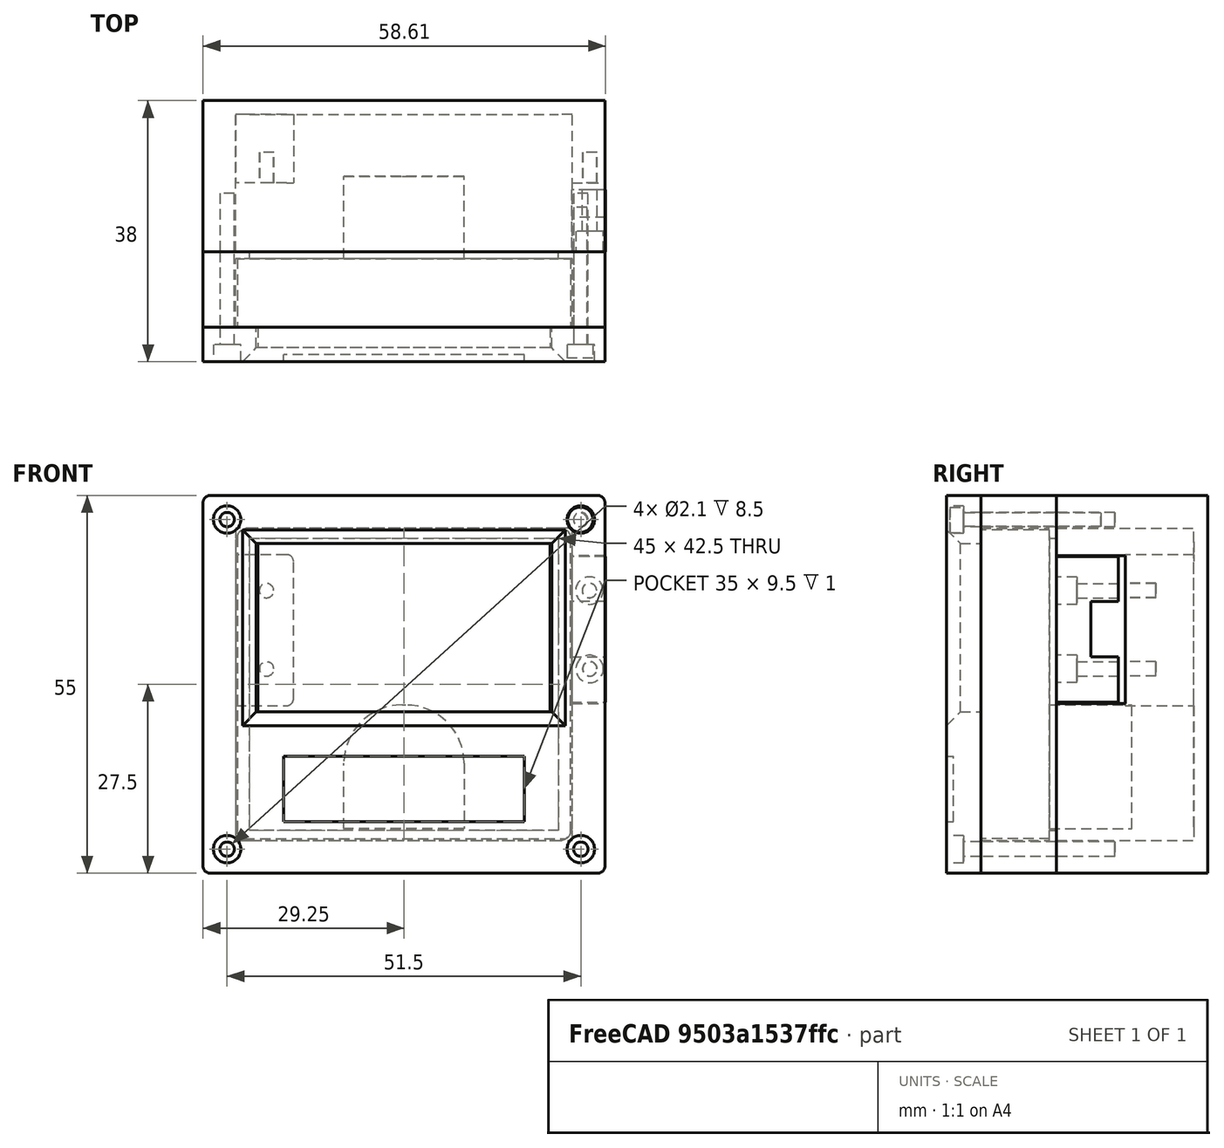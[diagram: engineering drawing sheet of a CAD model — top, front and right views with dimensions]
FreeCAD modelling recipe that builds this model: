
FCSTD DOCUMENT  (FreeCAD 0.21R33668 +26 (Git))
Label: nuvu-enclosure
License: All rights reserved
LicenseURL: http://en.wikipedia.org/wiki/All_rights_reserved
objects: Sketcher::SketchObject×24, PartDesign::Pocket×14, PartDesign::Pad×10, PartDesign::Fillet×8, PartDesign::Body×6, Mesh::Feature×2, PartDesign::Chamfer×1
note: 96 computed .brp shape members not serialized (recipe doc carries the construction recipe); baked Part::Feature solids carry a one-line shape summary decoded from their .brp

FEATURE [Sketcher::SketchObject] Sketch002
  FullyConstrained = true
  MapMode = 5
  Placement = pos=(0,0,0) rot=(1,0,0;1.5708rad)
  Support = -> [XZ_Plane]
  sketch-geometry (5):
    g0: LineSegment StartX=-24.25 StartY=22.5 StartZ=0 EndX=-24.25 EndY=-22.5 EndZ=0
    g1: LineSegment StartX=-24.25 StartY=-22.5 StartZ=0 EndX=24.25 EndY=-22.5 EndZ=0
    g2: LineSegment StartX=24.25 StartY=-22.5 StartZ=0 EndX=24.25 EndY=22.5 EndZ=0
    g3: LineSegment StartX=24.25 StartY=22.5 StartZ=0 EndX=-24.25 EndY=22.5 EndZ=0
    g4: GeomPoint X=0 Y=0 Z=0
  constraints (12):
    c: Coincident(g0,g1)
    c: Coincident(g1,g2)
    c: Coincident(g2,g3)
    c: Coincident(g3,g0)
    c: Horizontal(g1)
    c: Horizontal(g3)
    c: Vertical(g0)
    c: Vertical(g2)
    c: Symmetric(g1,g0,g4)
    c: Coincident(g4,g-1)
    c: DistanceY(g0,g0) = 45
    c: DistanceX(g3,g3) = 48.5
FEATURE [PartDesign::Pad] Pad
  Direction = (0,-1,-2e-16)
  Length = 10
  Length2 = 10
  Placement = pos=(0,0,0) rot=(1,0,0;1.5708rad)
  Profile = -> Sketch002
  ReferenceAxis = -> Sketch002 [N_Axis]
  Type = 0
FEATURE [Sketcher::SketchObject] Sketch003
  ExternalGeometry = -> [Pad]
  FullyConstrained = true
  MapMode = 5
  Placement = pos=(0,-10,-2.2e-15) rot=(1,0,0;1.5708rad)
  Support = -> [Pad]
  sketch-geometry (5):
    g0: LineSegment StartX=-21.25 StartY=20.5 StartZ=0 EndX=-21.25 EndY=-4 EndZ=0
    g1: LineSegment StartX=-21.25 StartY=-4 StartZ=0 EndX=21.25 EndY=-4 EndZ=0
    g2: LineSegment StartX=21.25 StartY=-4 StartZ=0 EndX=21.25 EndY=20.5 EndZ=0
    g3: LineSegment StartX=21.25 StartY=20.5 StartZ=0 EndX=-21.25 EndY=20.5 EndZ=0
    g4: GeomPoint X=0 Y=8.25 Z=0
  constraints (13):
    c: Coincident(g0,g1)
    c: Coincident(g1,g2)
    c: Coincident(g2,g3)
    c: Coincident(g3,g0)
    c: Horizontal(g1)
    c: Horizontal(g3)
    c: Vertical(g0)
    c: Vertical(g2)
    c: Symmetric(g1,g0,g4)
    c: PointOnObject(g4,g-2)
    c: DistanceY(g2,g-3) = 2
    c: DistanceX(g-3,g0) = 3
    c: DistanceY(g0,g0) = 24.5
FEATURE [PartDesign::Pad] Pad002
  BaseFeature = -> Pad
  Direction = (0,-1,-2e-16)
  Length = 3
  Length2 = 10
  Placement = pos=(0,0,0) rot=(1,0,0;1.5708rad)
  Profile = -> Sketch003
  ReferenceAxis = -> Sketch003 [N_Axis]
  Type = 0
FEATURE [Sketcher::SketchObject] Sketch004
  ExternalGeometry = -> [Pad002]
  FullyConstrained = true
  MapMode = 5
  Placement = pos=(0,0,0) rot=(-1,0,0;1.5708rad)
  Support = -> [Pad002]
  sketch-geometry (5):
    g0: LineSegment StartX=-8.75 StartY=21 StartZ=0 EndX=-8.75 EndY=3 EndZ=0
    g1: LineSegment StartX=-8.75 StartY=3 StartZ=0 EndX=8.75 EndY=3 EndZ=0
    g2: LineSegment StartX=8.75 StartY=3 StartZ=0 EndX=8.75 EndY=21 EndZ=0
    g3: LineSegment StartX=8.75 StartY=21 StartZ=0 EndX=-8.75 EndY=21 EndZ=0
    g4: GeomPoint X=0 Y=12 Z=0
  constraints (13):
    c: Coincident(g0,g1)
    c: Coincident(g1,g2)
    c: Coincident(g2,g3)
    c: Coincident(g3,g0)
    c: Horizontal(g1)
    c: Horizontal(g3)
    c: Vertical(g0)
    c: Vertical(g2)
    c: Symmetric(g1,g0,g4)
    c: PointOnObject(g4,g-2)
    c: DistanceX(g3,g3) = 17.5
    c: DistanceY(g2,g2) = 18
    c: DistanceY(g0,g-4) = 1.5
FEATURE [PartDesign::Pad] Pad003
  BaseFeature = -> Pad002
  Direction = (0,1,2e-16)
  Length = 12
  Length2 = 10
  Placement = pos=(0,0,0) rot=(1,0,0;1.5708rad)
  Profile = -> Sketch004
  ReferenceAxis = -> Sketch004 [N_Axis]
  Type = 0
FEATURE [PartDesign::Fillet] Fillet
  Base = -> Pad003 [Edge5,Edge8,Edge1,Edge2]
  BaseFeature = -> Pad003
  Placement = pos=(0,0,0) rot=(1,0,0;1.5708rad)
  Radius = 1
  SupportTransform = false
  UseAllEdges = false
FEATURE [PartDesign::Fillet] Fillet001
  Base = -> Fillet [Edge36,Edge34]
  BaseFeature = -> Fillet
  Placement = pos=(0,0,0) rot=(1,0,0;1.5708rad)
  Radius = 8.5
  SupportTransform = false
  UseAllEdges = false
FEATURE [PartDesign::Body] Body  label="VU Meter"
  Group = -> [Sketch002,Pad,Sketch003,Pad002,Sketch004,Pad003,Fillet,Fillet001]
  Origin = -> Origin
  Placement = pos=(0,10,0) rot=(0,0,1;0rad)
  Tip = -> Fillet001
FEATURE [Mesh::Feature] Raspberry_Pi_Pico_R3  label="Raspberry Pi Pico-R3"
  Placement = pos=(3.5,20.5,8) rot=(-0.707107,0,0.707107;3.14159rad)
FEATURE [Mesh::Feature] LED_5mm__RND_135_00125  label="LED_5mm__RND_135-00125"
  Placement = pos=(0,15.5,6) rot=(1,0,0;1.5708rad)
FEATURE [Sketcher::SketchObject] Sketch
  FullyConstrained = true
  MapMode = 5
  Placement = pos=(0,0,0) rot=(1,0,0;1.5708rad)
  Support = -> [XZ_Plane001]
  sketch-geometry (4):
    g0: LineSegment StartX=-29.25 StartY=27.5 StartZ=0 EndX=29.25 EndY=27.5 EndZ=0
    g1: LineSegment StartX=29.25 StartY=27.5 StartZ=0 EndX=29.25 EndY=-27.5 EndZ=0
    g2: LineSegment StartX=29.25 StartY=-27.5 StartZ=0 EndX=-29.25 EndY=-27.5 EndZ=0
    g3: LineSegment StartX=-29.25 StartY=-27.5 StartZ=0 EndX=-29.25 EndY=27.5 EndZ=0
  constraints (10):
    c: Coincident(g0,g1)
    c: Coincident(g1,g2)
    c: Coincident(g2,g3)
    c: Coincident(g3,g0)
    c: DistanceX(g0,g0) = 58.5
    c: DistanceY(g3,g3) = 55
    c: Symmetric(g2,g0,g-1)
    c: Symmetric(g0,g1,g-1)
    c: Vertical(g3)
    c: Horizontal(g0)
FEATURE [PartDesign::Pad] Pad004
  Direction = (0,-1,2e-16)
  Length = 5
  Length2 = 10
  Placement = pos=(0,0,0) rot=(1,0,0;1.5708rad)
  Profile = -> Sketch
  ReferenceAxis = -> Sketch [N_Axis]
  Type = 0
FEATURE [Sketcher::SketchObject] Sketch005
  ExternalGeometry = -> [Pad004]
  FullyConstrained = true
  MapMode = 5
  Placement = pos=(0,-5,1.1e-15) rot=(1,0,0;1.5708rad)
  Support = -> [Pad004]
  sketch-geometry (4):
    g0: LineSegment StartX=-21.5 StartY=20.5 StartZ=0 EndX=21.5 EndY=20.5 EndZ=0
    g1: LineSegment StartX=21.5 StartY=20.5 StartZ=0 EndX=21.5 EndY=-4 EndZ=0
    g2: LineSegment StartX=21.5 StartY=-4 StartZ=0 EndX=-21.5 EndY=-4 EndZ=0
    g3: LineSegment StartX=-21.5 StartY=-4 StartZ=0 EndX=-21.5 EndY=20.5 EndZ=0
  constraints (12):
    c: Coincident(g0,g1)
    c: Coincident(g1,g2)
    c: Coincident(g2,g3)
    c: Coincident(g3,g0)
    c: Horizontal(g0)
    c: Horizontal(g2)
    c: Vertical(g1)
    c: Vertical(g3)
    c: DistanceY(g3,g3) = 24.5
    c: DistanceX(g0,g0) = 43
    c: DistanceX(g-3,g0) = 7.75
    c: DistanceY(g0,g-3) = 7
FEATURE [PartDesign::Pocket] Pocket
  BaseFeature = -> Pad004
  Direction = (0,1,-2e-16)
  Length = 5
  Length2 = 5
  Placement = pos=(0,0,0) rot=(1,0,0;1.5708rad)
  Profile = -> Sketch005
  ReferenceAxis = -> Sketch005 [N_Axis]
  Type = 0
FEATURE [PartDesign::Chamfer] Chamfer
  Angle = 45
  Base = -> Pocket [Edge20,Edge17,Edge19,Edge18]
  BaseFeature = -> Pocket
  ChamferType = 0
  FlipDirection = false
  Placement = pos=(0,0,0) rot=(1,0,0;1.5708rad)
  Size = 2
  Size2 = 1
  SupportTransform = false
  UseAllEdges = false
FEATURE [Sketcher::SketchObject] Sketch006
  ExternalGeometry = -> [Chamfer]
  FullyConstrained = true
  MapMode = 5
  Placement = pos=(0,-5,1.1e-15) rot=(1,0,0;1.5708rad)
  Support = -> [Chamfer]
  sketch-geometry (4):
    g0: Circle CenterX=-25.75 CenterY=24 CenterZ=0 NormalX=0 NormalY=0 NormalZ=1 AngleXU=0 Radius=2
    g1: Circle CenterX=25.75 CenterY=24 CenterZ=0 NormalX=0 NormalY=0 NormalZ=1 AngleXU=0 Radius=2
    g2: Circle CenterX=-25.75 CenterY=-24 CenterZ=0 NormalX=0 NormalY=0 NormalZ=1 AngleXU=0 Radius=2
    g3: Circle CenterX=25.75 CenterY=-24 CenterZ=0 NormalX=0 NormalY=0 NormalZ=1 AngleXU=0 Radius=2
  constraints (12):
    c: Diameter(g0) = 4
    c: DistanceX(g-3,g0) = 3.5
    c: DistanceY(g0,g-3) = 3.5
    c: Diameter(g1) = 4
    c: DistanceX(g1,g-3) = 3.5
    c: DistanceY(g1,g-3) = 3.5
    c: Diameter(g2) = 4
    c: DistanceX(g-4,g2) = 3.5
    c: DistanceY(g-4,g2) = 3.5
    c: Diameter(g3) = 4
    c: DistanceY(g-4,g3) = 3.5
    c: DistanceX(g3,g-4) = 3.5
FEATURE [PartDesign::Pocket] Pocket001
  BaseFeature = -> Chamfer
  Direction = (0,1,-2e-16)
  Length = 2.5
  Length2 = 5
  Placement = pos=(0,0,0) rot=(1,0,0;1.5708rad)
  Profile = -> Sketch006
  ReferenceAxis = -> Sketch006 [N_Axis]
  Type = 0
FEATURE [Sketcher::SketchObject] Sketch007
  ExternalGeometry = -> [Pocket001]
  FullyConstrained = true
  MapMode = 5
  Placement = pos=(0,-2.5,6e-16) rot=(1,0,0;1.5708rad)
  Support = -> [Pocket001]
  sketch-geometry (4):
    g0: Circle CenterX=-25.75 CenterY=24 CenterZ=0 NormalX=0 NormalY=0 NormalZ=1 AngleXU=0 Radius=1.05
    g1: Circle CenterX=25.75 CenterY=24 CenterZ=0 NormalX=0 NormalY=0 NormalZ=1 AngleXU=0 Radius=1.05
    g2: Circle CenterX=25.75 CenterY=-24 CenterZ=0 NormalX=0 NormalY=0 NormalZ=1 AngleXU=0 Radius=1.05
    g3: Circle CenterX=-25.75 CenterY=-24 CenterZ=0 NormalX=0 NormalY=0 NormalZ=1 AngleXU=0 Radius=1.05
  constraints (8):
    c: Coincident(g0,g-3)
    c: Coincident(g1,g-4)
    c: Coincident(g2,g-6)
    c: Coincident(g3,g-5)
    c: Diameter(g0) = 2.1
    c: Diameter(g1) = 2.1
    c: Diameter(g3) = 2.1
    c: Diameter(g2) = 2.1
FEATURE [PartDesign::Pocket] Pocket002
  BaseFeature = -> Pocket001
  Direction = (0,1,-2e-16)
  Length = 5
  Length2 = 5
  Placement = pos=(0,0,0) rot=(1,0,0;1.5708rad)
  Profile = -> Sketch007
  ReferenceAxis = -> Sketch007 [N_Axis]
  Type = 0
FEATURE [Sketcher::SketchObject] Sketch008
  FullyConstrained = true
  MapMode = 5
  Placement = pos=(0,-5,1.1e-15) rot=(1,0,0;1.5708rad)
  Support = -> [Pocket002]
  sketch-geometry (5):
    g0: LineSegment StartX=-17.5 StartY=-10.5 StartZ=0 EndX=-17.5 EndY=-20 EndZ=0
    g1: LineSegment StartX=-17.5 StartY=-20 StartZ=0 EndX=17.5 EndY=-20 EndZ=0
    g2: LineSegment StartX=17.5 StartY=-20 StartZ=0 EndX=17.5 EndY=-10.5 EndZ=0
    g3: LineSegment StartX=17.5 StartY=-10.5 StartZ=0 EndX=-17.5 EndY=-10.5 EndZ=0
    g4: GeomPoint X=0 Y=-15.25 Z=0
  constraints (13):
    c: Coincident(g0,g1)
    c: Coincident(g1,g2)
    c: Coincident(g2,g3)
    c: Coincident(g3,g0)
    c: Horizontal(g1)
    c: Horizontal(g3)
    c: Vertical(g0)
    c: Vertical(g2)
    c: Symmetric(g1,g0,g4)
    c: PointOnObject(g4,g-2)
    c: DistanceX(g3,g3) = 35
    c: DistanceY(g2,g2) = 9.5
    c: DistanceY(g0,g-1) = 10.5
FEATURE [PartDesign::Pocket] Pocket003
  BaseFeature = -> Pocket002
  Direction = (0,1,-2e-16)
  Length = 1
  Length2 = 5
  Placement = pos=(0,0,0) rot=(1,0,0;1.5708rad)
  Profile = -> Sketch008
  ReferenceAxis = -> Sketch008 [N_Axis]
  Type = 0
FEATURE [PartDesign::Fillet] Fillet002
  Base = -> Pocket003 [Edge18,Edge17,Edge22,Edge20]
  BaseFeature = -> Pocket003
  Placement = pos=(0,0,0) rot=(1,0,0;1.5708rad)
  Radius = 1
  SupportTransform = false
  UseAllEdges = false
FEATURE [PartDesign::Body] Body001  label="Faceplate"
  Group = -> [Sketch,Pad004,Sketch005,Pocket,Chamfer,Sketch006,Pocket001,Sketch007,Pocket002,Sketch008,Pocket003,Fillet002]
  Origin = -> Origin001
  Tip = -> Fillet002
FEATURE [Sketcher::SketchObject] Sketch009
  FullyConstrained = true
  MapMode = 5
  Placement = pos=(0,0,0) rot=(1,0,0;1.5708rad)
  Support = -> [XZ_Plane002]
  sketch-geometry (5):
    g0: LineSegment StartX=-29.25 StartY=27.5 StartZ=0 EndX=-29.25 EndY=-27.5 EndZ=0
    g1: LineSegment StartX=-29.25 StartY=-27.5 StartZ=0 EndX=29.25 EndY=-27.5 EndZ=0
    g2: LineSegment StartX=29.25 StartY=-27.5 StartZ=0 EndX=29.25 EndY=27.5 EndZ=0
    g3: LineSegment StartX=29.25 StartY=27.5 StartZ=0 EndX=-29.25 EndY=27.5 EndZ=0
    g4: GeomPoint X=0 Y=0 Z=0
  constraints (12):
    c: Coincident(g0,g1)
    c: Coincident(g1,g2)
    c: Coincident(g2,g3)
    c: Coincident(g3,g0)
    c: Horizontal(g1)
    c: Horizontal(g3)
    c: Vertical(g0)
    c: Vertical(g2)
    c: Symmetric(g1,g0,g4)
    c: Coincident(g4,g-1)
    c: DistanceX(g3,g3) = 58.5
    c: DistanceY(g2,g2) = 55
FEATURE [PartDesign::Pad] Pad005
  Direction = (0,-1,2e-16)
  Length = 11
  Length2 = 10
  Placement = pos=(0,0,0) rot=(1,0,0;1.5708rad)
  Profile = -> Sketch009
  ReferenceAxis = -> Sketch009 [N_Axis]
  Reversed = true
  Type = 0
FEATURE [Sketcher::SketchObject] Sketch010
  FullyConstrained = true
  MapMode = 5
  Placement = pos=(0,0,0) rot=(1,0,0;1.5708rad)
  Support = -> [Pad005]
  sketch-geometry (5):
    g0: LineSegment StartX=-24.5 StartY=22.75 StartZ=0 EndX=-24.5 EndY=-22.75 EndZ=0
    g1: LineSegment StartX=-24.5 StartY=-22.75 StartZ=0 EndX=24.5 EndY=-22.75 EndZ=0
    g2: LineSegment StartX=24.5 StartY=-22.75 StartZ=0 EndX=24.5 EndY=22.75 EndZ=0
    g3: LineSegment StartX=24.5 StartY=22.75 StartZ=0 EndX=-24.5 EndY=22.75 EndZ=0
    g4: GeomPoint X=0 Y=0 Z=0
  constraints (12):
    c: Coincident(g0,g1)
    c: Coincident(g1,g2)
    c: Coincident(g2,g3)
    c: Coincident(g3,g0)
    c: Horizontal(g1)
    c: Horizontal(g3)
    c: Vertical(g0)
    c: Vertical(g2)
    c: Symmetric(g1,g0,g4)
    c: Coincident(g4,g-1)
    c: DistanceX(g3,g3) = 49
    c: DistanceY(g0,g0) = 45.5
FEATURE [PartDesign::Pocket] Pocket004
  BaseFeature = -> Pad005
  Direction = (0,1,-2e-16)
  Length = 10
  Length2 = 5
  Placement = pos=(0,0,0) rot=(1,0,0;1.5708rad)
  Profile = -> Sketch010
  ReferenceAxis = -> Sketch010 [N_Axis]
  Type = 0
FEATURE [Sketcher::SketchObject] Sketch011
  ExternalGeometry = -> [Pocket004]
  FullyConstrained = true
  MapMode = 5
  Placement = pos=(0,10,-2.2e-15) rot=(1,0,0;1.5708rad)
  Support = -> [Pocket004]
  sketch-geometry (5):
    g0: LineSegment StartX=-22.5 StartY=21.25 StartZ=0 EndX=-22.5 EndY=-21.25 EndZ=0
    g1: LineSegment StartX=-22.5 StartY=-21.25 StartZ=0 EndX=22.5 EndY=-21.25 EndZ=0
    g2: LineSegment StartX=22.5 StartY=-21.25 StartZ=0 EndX=22.5 EndY=21.25 EndZ=0
    g3: LineSegment StartX=22.5 StartY=21.25 StartZ=0 EndX=-22.5 EndY=21.25 EndZ=0
    g4: GeomPoint X=0 Y=0 Z=0
  constraints (12):
    c: Coincident(g0,g1)
    c: Coincident(g1,g2)
    c: Coincident(g2,g3)
    c: Coincident(g3,g0)
    c: Horizontal(g1)
    c: Horizontal(g3)
    c: Vertical(g0)
    c: Vertical(g2)
    c: Symmetric(g1,g0,g4)
    c: Coincident(g4,g-1)
    c: DistanceX(g-3,g0) = 2
    c: DistanceY(g0,g-3) = 1.5
FEATURE [PartDesign::Pocket] Pocket005
  BaseFeature = -> Pocket004
  Direction = (0,1,-2e-16)
  Length = 5
  Length2 = 5
  Placement = pos=(0,0,0) rot=(1,0,0;1.5708rad)
  Profile = -> Sketch011
  ReferenceAxis = -> Sketch011 [N_Axis]
  Type = 0
FEATURE [Sketcher::SketchObject] Sketch012
  ExternalGeometry = -> [Pocket005]
  FullyConstrained = true
  MapMode = 5
  Placement = pos=(0,0,0) rot=(1,0,0;1.5708rad)
  Support = -> [Pocket005]
  sketch-geometry (4):
    g0: Circle CenterX=-25.75 CenterY=24 CenterZ=0 NormalX=0 NormalY=0 NormalZ=1 AngleXU=0 Radius=1.05
    g1: Circle CenterX=25.75 CenterY=24 CenterZ=0 NormalX=0 NormalY=0 NormalZ=1 AngleXU=0 Radius=1.05
    g2: Circle CenterX=-25.75 CenterY=-24 CenterZ=0 NormalX=0 NormalY=0 NormalZ=1 AngleXU=0 Radius=1.05
    g3: Circle CenterX=25.75 CenterY=-24 CenterZ=0 NormalX=0 NormalY=0 NormalZ=1 AngleXU=0 Radius=1.05
  constraints (12):
    c: Diameter(g0) = 2.1
    c: DistanceX(g-3,g0) = 3.5
    c: DistanceY(g0,g-3) = 3.5
    c: Diameter(g1) = 2.1
    c: DistanceX(g1,g-3) = 3.5
    c: DistanceY(g1,g-3) = 3.5
    c: Diameter(g2) = 2.1
    c: Diameter(g3) = 2.1
    c: DistanceY(g-4,g2) = 3.5
    c: DistanceY(g-4,g3) = 3.5
    c: DistanceX(g-4,g2) = 3.5
    c: DistanceX(g3,g-4) = 3.5
FEATURE [PartDesign::Pocket] Pocket006
  BaseFeature = -> Pocket005
  Direction = (0,1,-2e-16)
  Length = 12
  Length2 = 5
  Placement = pos=(0,0,0) rot=(1,0,0;1.5708rad)
  Profile = -> Sketch012
  ReferenceAxis = -> Sketch012 [N_Axis]
  Type = 0
FEATURE [PartDesign::Fillet] Fillet003
  Base = -> Pocket006 [Edge5,Edge8,Edge1,Edge2]
  BaseFeature = -> Pocket006
  Placement = pos=(0,0,0) rot=(1,0,0;1.5708rad)
  Radius = 1
  SupportTransform = false
  UseAllEdges = false
FEATURE [PartDesign::Body] Body002  label="VU Meter Retainer"
  Group = -> [Sketch009,Pad005,Sketch010,Pocket004,Sketch011,Pocket005,Sketch012,Pocket006,Fillet003]
  Origin = -> Origin002
  Tip = -> Fillet003
FEATURE [Sketcher::SketchObject] Sketch013
  FullyConstrained = false
  MapMode = 5
  Placement = pos=(0,0,0) rot=(1,0,0;1.5708rad)
  Support = -> [XZ_Plane003]
  sketch-geometry (1):
    g0: Circle CenterX=19.6771 CenterY=42.9655 CenterZ=0 NormalX=0 NormalY=0 NormalZ=1 AngleXU=0 Radius=1.85
  constraints (1):
    c: Diameter(g0) = 3.7
FEATURE [PartDesign::Pad] Pad006
  Direction = (0,-1,2e-16)
  Length = 2
  Length2 = 10
  Placement = pos=(0,0,0) rot=(1,0,0;1.5708rad)
  Profile = -> Sketch013
  ReferenceAxis = -> Sketch013 [N_Axis]
  Type = 0
FEATURE [Sketcher::SketchObject] Sketch014
  ExternalGeometry = -> [Pad006]
  FullyConstrained = true
  MapMode = 5
  Placement = pos=(0,0,0) rot=(-1,0,0;1.5708rad)
  Support = -> [Pad006]
  sketch-geometry (1):
    g0: Circle CenterX=19.6771 CenterY=-42.9655 CenterZ=0 NormalX=0 NormalY=0 NormalZ=1 AngleXU=0 Radius=1
  constraints (2):
    c: Coincident(g0,g-3)
    c: Diameter(g0) = 2
FEATURE [PartDesign::Pad] Pad007
  BaseFeature = -> Pad006
  Direction = (0,1,-2e-16)
  Length = 20
  Length2 = 10
  Placement = pos=(0,0,0) rot=(1,0,0;1.5708rad)
  Profile = -> Sketch014
  ReferenceAxis = -> Sketch014 [N_Axis]
  Type = 0
FEATURE [PartDesign::Body] Body003  label="Bolt"
  Group = -> [Sketch013,Pad006,Sketch014,Pad007]
  Origin = -> Origin003
  Placement = pos=(6,-2.5,-19) rot=(0,0,1;0rad)
  Tip = -> Pad007
FEATURE [Sketcher::SketchObject] Sketch015
  FullyConstrained = true
  MapMode = 5
  Placement = pos=(0,0,0) rot=(1,0,0;1.5708rad)
  Support = -> [XZ_Plane004]
  sketch-geometry (5):
    g0: LineSegment StartX=29.25 StartY=27.5 StartZ=0 EndX=29.25 EndY=-27.5 EndZ=0
    g1: LineSegment StartX=29.25 StartY=-27.5 StartZ=0 EndX=-29.25 EndY=-27.5 EndZ=0
    g2: LineSegment StartX=-29.25 StartY=-27.5 StartZ=0 EndX=-29.25 EndY=27.5 EndZ=0
    g3: LineSegment StartX=-29.25 StartY=27.5 StartZ=0 EndX=29.25 EndY=27.5 EndZ=0
    g4: GeomPoint X=0 Y=0 Z=0
  constraints (12):
    c: Coincident(g0,g1)
    c: Coincident(g1,g2)
    c: Coincident(g2,g3)
    c: Coincident(g3,g0)
    c: Horizontal(g1)
    c: Horizontal(g3)
    c: Vertical(g0)
    c: Vertical(g2)
    c: Symmetric(g1,g0,g4)
    c: Coincident(g4,g-1)
    c: DistanceX(g3,g3) = 58.5
    c: DistanceY(g2,g2) = 55
FEATURE [PartDesign::Pad] Pad008
  Direction = (0,-1,2e-16)
  Length = 22
  Length2 = 10
  Placement = pos=(0,0,0) rot=(1,0,0;1.5708rad)
  Profile = -> Sketch015
  ReferenceAxis = -> Sketch015 [N_Axis]
  Type = 0
FEATURE [Sketcher::SketchObject] Sketch016
  FullyConstrained = true
  MapMode = 5
  Placement = pos=(0,-22,4.9e-15) rot=(1,0,0;1.5708rad)
  Support = -> [Pad008]
  sketch-geometry (5):
    g0: LineSegment StartX=-24.5 StartY=22.75 StartZ=0 EndX=-24.5 EndY=-22.75 EndZ=0
    g1: LineSegment StartX=-24.5 StartY=-22.75 StartZ=0 EndX=24.5 EndY=-22.75 EndZ=0
    g2: LineSegment StartX=24.5 StartY=-22.75 StartZ=0 EndX=24.5 EndY=22.75 EndZ=0
    g3: LineSegment StartX=24.5 StartY=22.75 StartZ=0 EndX=-24.5 EndY=22.75 EndZ=0
    g4: GeomPoint X=0 Y=0 Z=0
  constraints (12):
    c: Coincident(g0,g1)
    c: Coincident(g1,g2)
    c: Coincident(g2,g3)
    c: Coincident(g3,g0)
    c: Horizontal(g1)
    c: Horizontal(g3)
    c: Vertical(g0)
    c: Vertical(g2)
    c: Symmetric(g1,g0,g4)
    c: Coincident(g4,g-1)
    c: DistanceX(g3,g3) = 49
    c: DistanceY(g0,g0) = 45.5
FEATURE [PartDesign::Pocket] Pocket007
  BaseFeature = -> Pad008
  Direction = (0,1,-2e-16)
  Length = 20
  Length2 = 5
  Placement = pos=(0,0,0) rot=(1,0,0;1.5708rad)
  Profile = -> Sketch016
  ReferenceAxis = -> Sketch016 [N_Axis]
  Type = 0
FEATURE [Sketcher::SketchObject] Sketch017
  ExternalGeometry = -> [Pocket007]
  FullyConstrained = true
  MapMode = 5
  Placement = pos=(0,-22,4.9e-15) rot=(1,0,0;1.5708rad)
  Support = -> [Pocket007]
  sketch-geometry (4):
    g0: LineSegment StartX=30.8 StartY=18.71 StartZ=0 EndX=22.8 EndY=18.71 EndZ=0
    g1: LineSegment StartX=22.8 StartY=18.71 StartZ=0 EndX=22.8 EndY=-2.79 EndZ=0
    g2: LineSegment StartX=22.8 StartY=-2.79 StartZ=0 EndX=30.8 EndY=-2.79 EndZ=0
    g3: LineSegment StartX=30.8 StartY=-2.79 StartZ=0 EndX=30.8 EndY=18.71 EndZ=0
  constraints (12):
    c: Coincident(g0,g1)
    c: Coincident(g1,g2)
    c: Coincident(g2,g3)
    c: Coincident(g3,g0)
    c: Horizontal(g0)
    c: Horizontal(g2)
    c: Vertical(g1)
    c: Vertical(g3)
    c: DistanceX(g0,g0) = 8
    c: DistanceY(g1,g1) = 21.5
    c: DistanceX(g-3,g0) = 1.55
    c: DistanceY(g0,g-3) = 8.79
FEATURE [PartDesign::Pocket] Pocket008
  BaseFeature = -> Pocket007
  Direction = (0,1,-2e-16)
  Length = 10
  Length2 = 5
  Placement = pos=(0,0,0) rot=(1,0,0;1.5708rad)
  Profile = -> Sketch017
  ReferenceAxis = -> Sketch017 [N_Axis]
  Type = 0
FEATURE [Sketcher::SketchObject] Sketch019
  FullyConstrained = false
  MapMode = 5
  Placement = pos=(0,-2,3e-16) rot=(1,0,0;1.5708rad)
  sketch-geometry (5):
    g0: LineSegment StartX=-24.87 StartY=18.89 StartZ=0 EndX=-24.87 EndY=-3.11 EndZ=0
    g1: LineSegment StartX=-24.87 StartY=-3.11 StartZ=0 EndX=-16.09 EndY=-3.11 EndZ=0
    g2: LineSegment StartX=-16.09 StartY=-3.11 StartZ=0 EndX=-16.09 EndY=18.89 EndZ=0
    g3: LineSegment StartX=-16.09 StartY=18.89 StartZ=0 EndX=-24.87 EndY=18.89 EndZ=0
    g4: GeomPoint X=-20.48 Y=7.89 Z=0
  constraints (11):
    c: Coincident(g0,g1)
    c: Coincident(g1,g2)
    c: Coincident(g2,g3)
    c: Coincident(g3,g0)
    c: Horizontal(g1)
    c: Horizontal(g3)
    c: Vertical(g0)
    c: Vertical(g2)
    c: Symmetric(g1,g0,g4)
    c: DistanceX(g3,g3) = 8.78
    c: DistanceY(g2,g2) = 22
FEATURE [PartDesign::Pad] Pad009
  BaseFeature = -> Pocket008
  Direction = (0,-1,2e-16)
  Length = 10
  Length2 = 10
  Placement = pos=(0,0,0) rot=(1,0,0;1.5708rad)
  Profile = -> Sketch019
  ReferenceAxis = -> Sketch019 [N_Axis]
  Type = 0
FEATURE [Sketcher::SketchObject] Sketch020
  FullyConstrained = true
  MapMode = 5
  Placement = pos=(0,0,0) rot=(1,0,0;1.5708rad)
  Support = -> [XZ_Plane005]
  sketch-geometry (5):
    g0: LineSegment StartX=24.3594 StartY=18.5816 StartZ=0 EndX=24.3594 EndY=-2.61844 EndZ=0
    g1: LineSegment StartX=24.3594 StartY=-2.61844 StartZ=0 EndX=29.3594 EndY=-2.61844 EndZ=0
    g2: LineSegment StartX=29.3594 StartY=-2.61844 StartZ=0 EndX=29.3594 EndY=18.5816 EndZ=0
    g3: LineSegment StartX=29.3594 StartY=18.5816 StartZ=0 EndX=24.3594 EndY=18.5816 EndZ=0
    g4: GeomPoint X=26.8594 Y=7.98156 Z=0
  constraints (12):
    c: Coincident(g0,g1)
    c: Coincident(g1,g2)
    c: Coincident(g2,g3)
    c: Coincident(g3,g0)
    c: Horizontal(g1)
    c: Horizontal(g3)
    c: Vertical(g0)
    c: Vertical(g2)
    c: Symmetric(g1,g0,g4)
    c: DistanceX(g3,g3) = 5
    c: DistanceY(g0,g0) = 21.2
    c: Block(g0)
FEATURE [PartDesign::Pad] Pad010
  Direction = (0,-1,2e-16)
  Length = 9
  Length2 = 10
  Placement = pos=(0,0,0) rot=(1,0,0;1.5708rad)
  Profile = -> Sketch020
  ReferenceAxis = -> Sketch020 [N_Axis]
  Type = 0
FEATURE [Sketcher::SketchObject] Sketch021
  FullyConstrained = false
  MapMode = 5
  Placement = pos=(0,-12,2e-15) rot=(1,0,0;1.5708rad)
  sketch-geometry (6):
    g0: Circle CenterX=26.9984 CenterY=13.6609 CenterZ=0 NormalX=0 NormalY=0 NormalZ=1 AngleXU=0 Radius=1.05
    g1: Circle CenterX=27.0804 CenterY=2.26094 CenterZ=0 NormalX=0 NormalY=0 NormalZ=1 AngleXU=0 Radius=1.05
    g2: Circle CenterX=-20.0144 CenterY=13.6419 CenterZ=0 NormalX=0 NormalY=0 NormalZ=1 AngleXU=0 Radius=1.05
    g3: Circle CenterX=-19.9983 CenterY=2.24187 CenterZ=0 NormalX=0 NormalY=0 NormalZ=1 AngleXU=0 Radius=1.05
    g4: LineSegment StartX=-22.0144 StartY=18.4102 StartZ=0 EndX=-22.0144 EndY=-2.43807 EndZ=0
    g5: LineSegment StartX=28.9984 StartY=18.4426 StartZ=0 EndX=28.9984 EndY=-2.43927 EndZ=0
  constraints (12):
    c: DistanceY(g1,g0) = 11.4
    c: DistanceY(g3,g2) = 11.4
    c: Vertical(g4)
    c: Vertical(g5)
    c: Block(g5)
    c: DistanceX(g0,g5) = 2
    c: Block(g4)
    c: DistanceX(g4,g2) = 2
    c: Diameter(g2) = 2.1
    c: Diameter(g3) = 2.1
    c: Diameter(g1) = 2.1
    c: Diameter(g0) = 2.1
FEATURE [PartDesign::Fillet] Fillet005
  Base = -> Pad009
  BaseFeature = -> Pad009
  Placement = pos=(0,0,0) rot=(1,0,0;1.5708rad)
  Radius = 1
  SupportTransform = false
  UseAllEdges = false
FEATURE [PartDesign::Pocket] Pocket009
  BaseFeature = -> Fillet005
  Direction = (0,1,-2e-16)
  Length = 4.5
  Length2 = 5
  Placement = pos=(0,0,0) rot=(1,0,0;1.5708rad)
  Profile = -> Sketch021
  ReferenceAxis = -> Sketch021 [N_Axis]
  Type = 0
FEATURE [PartDesign::Fillet] Fillet006
  Base = -> Pocket009 [Edge41,Edge31,Edge34,Edge33]
  BaseFeature = -> Pocket009
  Placement = pos=(0,0,0) rot=(1,0,0;1.5708rad)
  Radius = 2
  SupportTransform = false
  UseAllEdges = false
FEATURE [Sketcher::SketchObject] Sketch022
  ExternalGeometry = -> [Fillet006]
  FullyConstrained = true
  MapMode = 5
  Placement = pos=(0,-22,4.9e-15) rot=(1,0,0;1.5708rad)
  Support = -> [Fillet006]
  sketch-geometry (4):
    g0: Circle CenterX=-25.75 CenterY=24 CenterZ=0 NormalX=0 NormalY=0 NormalZ=1 AngleXU=0 Radius=1.05
    g1: Circle CenterX=25.75 CenterY=24 CenterZ=0 NormalX=0 NormalY=0 NormalZ=1 AngleXU=0 Radius=1.05
    g2: Circle CenterX=25.75 CenterY=-24 CenterZ=0 NormalX=0 NormalY=0 NormalZ=1 AngleXU=0 Radius=1.05
    g3: Circle CenterX=-25.75 CenterY=-24 CenterZ=0 NormalX=0 NormalY=0 NormalZ=1 AngleXU=0 Radius=1.05
  constraints (12):
    c: Diameter(g0) = 2.1
    c: Diameter(g1) = 2.1
    c: Diameter(g2) = 2.1
    c: Diameter(g3) = 2.1
    c: DistanceX(g-3,g0) = 3.5
    c: DistanceY(g0,g-3) = 3.5
    c: DistanceY(g1,g-3) = 3.5
    c: DistanceY(g-4,g3) = 3.5
    c: DistanceY(g-4,g2) = 3.5
    c: DistanceX(g1,g-3) = 3.5
    c: DistanceX(g2,g-4) = 3.5
    c: DistanceX(g-4,g3) = 3.5
FEATURE [PartDesign::Pocket] Pocket010
  BaseFeature = -> Fillet006
  Direction = (0,1,-2e-16)
  Length = 8.5
  Length2 = 5
  Placement = pos=(0,0,0) rot=(1,0,0;1.5708rad)
  Profile = -> Sketch022
  ReferenceAxis = -> Sketch022 [N_Axis]
  Type = 0
FEATURE [PartDesign::Fillet] Fillet007
  Base = -> Pocket010 [Edge72,Edge71]
  BaseFeature = -> Pocket010
  Placement = pos=(0,0,0) rot=(1,0,0;1.5708rad)
  Radius = 1
  SupportTransform = false
  UseAllEdges = false
FEATURE [PartDesign::Fillet] Fillet008
  Base = -> Fillet007 [Edge73,Edge72,Edge74,Edge76]
  BaseFeature = -> Fillet007
  Placement = pos=(0,0,0) rot=(1,0,0;1.5708rad)
  Radius = 1
  SupportTransform = false
  UseAllEdges = false
FEATURE [PartDesign::Body] Body004  label="Back"
  Group = -> [Sketch015,Pad008,Sketch016,Pocket007,Sketch017,Pocket008,Sketch019,Pad009,Sketch021,Fillet005,Pocket009,Fillet006,Sketch022,Pocket010,Fillet007,Fillet008]
  Origin = -> Origin004
  Placement = pos=(0,33,0) rot=(0,0,1;0rad)
  Tip = -> Fillet008
FEATURE [Sketcher::SketchObject] Sketch023
  FullyConstrained = false
  MapMode = 5
  Placement = pos=(0,0,0) rot=(-1,0,0;1.5708rad)
  Support = -> [Pad010]
  sketch-geometry (4):
    g0: LineSegment StartX=30.5369 StartY=-12.0845 StartZ=0 EndX=23.8869 EndY=-12.0845 EndZ=0
    g1: LineSegment StartX=23.8869 StartY=-12.0845 StartZ=0 EndX=23.8869 EndY=-3.98451 EndZ=0
    g2: LineSegment StartX=23.8869 StartY=-3.98451 StartZ=0 EndX=30.5369 EndY=-3.98451 EndZ=0
    g3: LineSegment StartX=30.5369 StartY=-3.98451 StartZ=0 EndX=30.5369 EndY=-12.0845 EndZ=0
  constraints (10):
    c: Coincident(g0,g1)
    c: Coincident(g1,g2)
    c: Coincident(g2,g3)
    c: Coincident(g3,g0)
    c: Horizontal(g0)
    c: Horizontal(g2)
    c: Vertical(g1)
    c: Vertical(g3)
    c: DistanceX(g0,g0) = 6.65
    c: DistanceY(g1,g1) = 8.1
FEATURE [PartDesign::Pocket] Pocket011
  BaseFeature = -> Pad010
  Direction = (0,-1,2e-16)
  Length = 4
  Length2 = 5
  Placement = pos=(0,0,0) rot=(1,0,0;1.5708rad)
  Profile = -> Sketch023
  ReferenceAxis = -> Sketch023 [N_Axis]
  Type = 0
FEATURE [Sketcher::SketchObject] Sketch024
  FullyConstrained = false
  MapMode = 5
  Placement = pos=(0,0,0) rot=(-1,0,0;1.5708rad)
  Support = -> [Pocket011]
  sketch-geometry (2):
    g0: Circle CenterX=27.0092 CenterY=-13.6509 CenterZ=0 NormalX=0 NormalY=0 NormalZ=1 AngleXU=0 Radius=1.05
    g1: Circle CenterX=27.0367 CenterY=-2.24397 CenterZ=0 NormalX=0 NormalY=0 NormalZ=1 AngleXU=0 Radius=1.05
  constraints (2):
    c: Diameter(g0) = 2.1
    c: Diameter(g1) = 2.1
FEATURE [PartDesign::Pocket] Pocket012
  BaseFeature = -> Pocket011
  Direction = (0,-1,2e-16)
  Length = 10
  Length2 = 5
  Placement = pos=(0,0,0) rot=(1,0,0;1.5708rad)
  Profile = -> Sketch024
  ReferenceAxis = -> Sketch024 [N_Axis]
  Type = 0
FEATURE [Sketcher::SketchObject] Sketch025
  ExternalGeometry = -> [Pocket012]
  FullyConstrained = true
  MapMode = 5
  Placement = pos=(0,-9,2e-15) rot=(1,0,0;1.5708rad)
  Support = -> [Pocket012]
  sketch-geometry (2):
    g0: Circle CenterX=27.0092 CenterY=13.6509 CenterZ=0 NormalX=0 NormalY=0 NormalZ=1 AngleXU=0 Radius=2
    g1: Circle CenterX=27.0367 CenterY=2.24397 CenterZ=0 NormalX=0 NormalY=0 NormalZ=1 AngleXU=0 Radius=2
  constraints (4):
    c: Coincident(g0,g-3)
    c: Coincident(g1,g-4)
    c: Diameter(g0) = 4
    c: Diameter(g1) = 4
FEATURE [PartDesign::Pocket] Pocket013
  BaseFeature = -> Pocket012
  Direction = (0,1,-2e-16)
  Length = 3
  Length2 = 5
  Placement = pos=(0,0,0) rot=(1,0,0;1.5708rad)
  Profile = -> Sketch025
  ReferenceAxis = -> Sketch025 [N_Axis]
  Type = 0
FEATURE [PartDesign::Body] Body005  label="Filler Panel"
  Group = -> [Sketch020,Pad010,Sketch023,Pocket011,Sketch024,Pocket012,Sketch025,Pocket013]
  Origin = -> Origin005
  Placement = pos=(0,20,0) rot=(0,0,1;0rad)
  Tip = -> Pocket013
